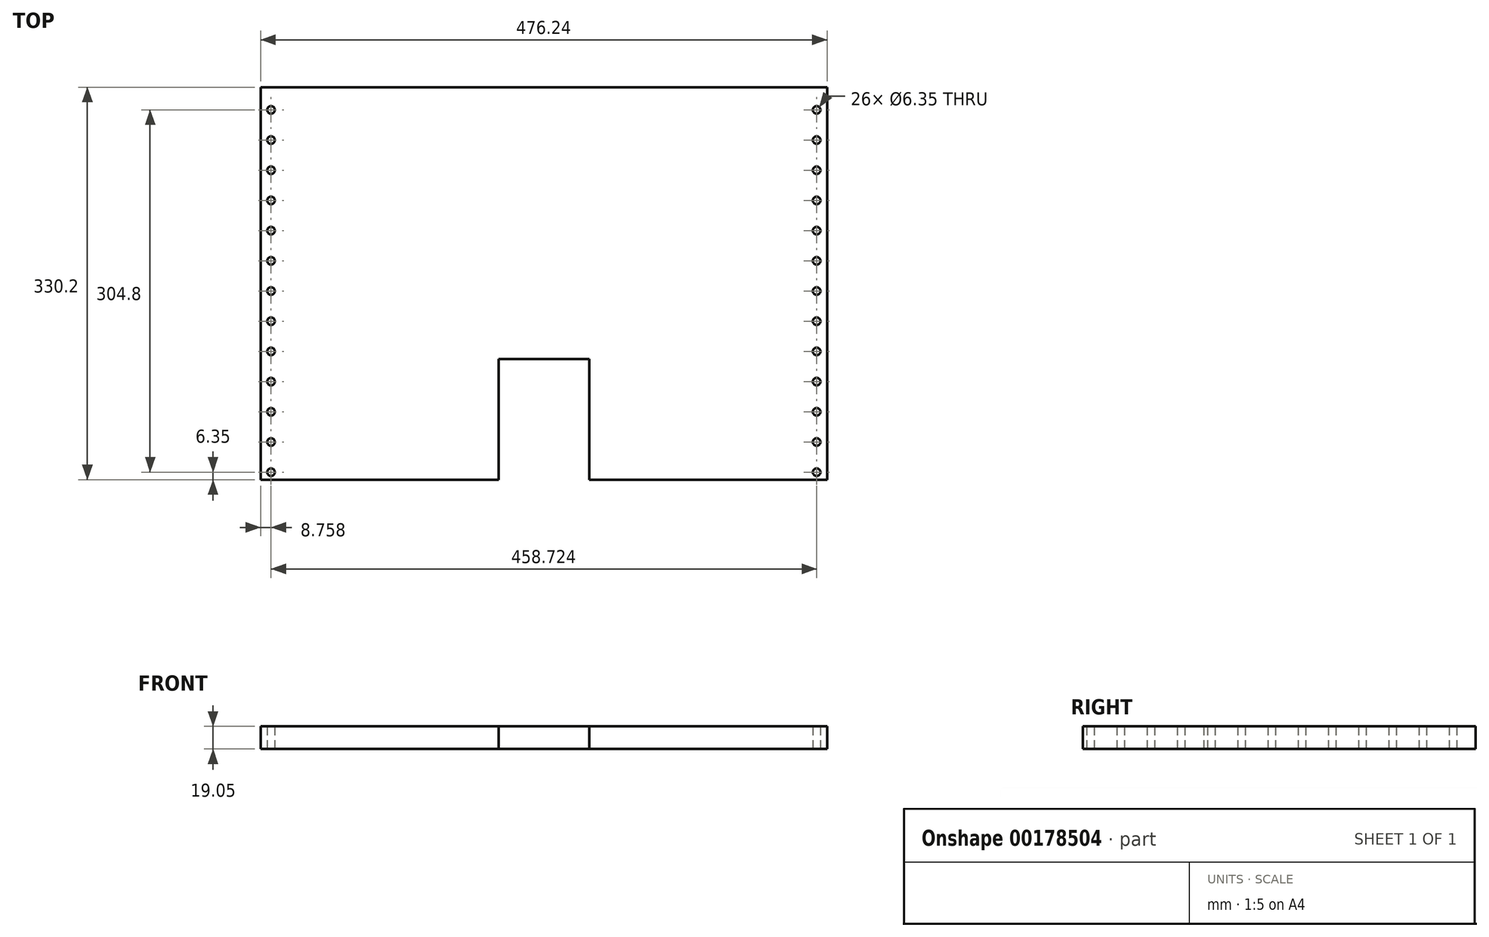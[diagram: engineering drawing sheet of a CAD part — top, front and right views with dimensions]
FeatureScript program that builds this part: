
annotation { "Feature Type Name" : "Feature", "Feature Type Description" : "" }
export const myFeature = defineFeature(function(context is Context, id is Id, definition is map)
    precondition{}
    {
        {
            var Q0;
            Q0=qCreatedBy(makeId("Top.planeOp"),FACE);
            var sketch = newSketch(context, id + "F0", { "sketchPlane" : qUnion([Q0])});
            skLineSegment(sketch, "E0.bottom", {"start": v(-238.13, 165.1) * mm, "end": v(238.13, 165.1) * mm});
            skLineSegment(sketch, "E0.top", {"start": v(-238.13, -165.1) * mm, "end": v(238.13, -165.1) * mm});
            skLineSegment(sketch, "E0.left", {"start": v(-238.13, 165.1) * mm, "end": v(-238.13, -165.1) * mm});
            skLineSegment(sketch, "E0.right", {"start": v(238.13, 165.1) * mm, "end": v(238.13, -165.1) * mm});
            skPoint(sketch, "E0.middle", {"position": v(0, 0) * mm});
            skPoint(sketch, "E1", {"position": v(0, 165.1) * mm});
            skLineSegment(sketch, "E2", {"start": v(0, 165.1) * mm, "end": v(0, -165.1) * mm});
            skLineSegment(sketch, "E3", {"start": v(0, -165.1) * mm, "end": v(-38.1, -165.1) * mm});
            skLineSegment(sketch, "E4", {"start": v(-38.1, -165.1) * mm, "end": v(-38.1, -63.5) * mm});
            skLineSegment(sketch, "E5", {"start": v(-38.1, -63.5) * mm, "end": v(0, -63.5) * mm});
            skLineSegment(sketch, "E6.MirrorCS", {"start": v(38.1, -63.5) * mm, "end": v(0, -63.5) * mm});
            skLineSegment(sketch, "E7.MirrorCS", {"start": v(38.1, -165.1) * mm, "end": v(38.1, -63.5) * mm});
            skLineSegment(sketch, "E8.MirrorCS", {"start": v(0, -165.1) * mm, "end": v(38.1, -165.1) * mm});
            skPoint(sketch, "E9", {"position": v(223.01, -165.1) * mm});
            skLineSegment(sketch, "E10", {"start": v(223.01, -165.1) * mm, "end": v(223.01, 165.1) * mm});
            skCircle(sketch, "E11", {"center": v(229.36, -158.75) * mm, "radius": 3.18 * mm});
            skCircle(sketch, "E12.0.1.0", {"center": v(229.36, -133.35) * mm, "radius": 3.18 * mm});
            skCircle(sketch, "E12.0.2.0", {"center": v(229.36, -107.95) * mm, "radius": 3.18 * mm});
            skCircle(sketch, "E12.0.3.0", {"center": v(229.36, -82.55) * mm, "radius": 3.18 * mm});
            skCircle(sketch, "E12.0.4.0", {"center": v(229.36, -57.15) * mm, "radius": 3.18 * mm});
            skCircle(sketch, "E12.0.5.0", {"center": v(229.36, -31.75) * mm, "radius": 3.18 * mm});
            skCircle(sketch, "E12.0.6.0", {"center": v(229.36, -6.35) * mm, "radius": 3.18 * mm});
            skCircle(sketch, "E12.0.7.0", {"center": v(229.36, 19.05) * mm, "radius": 3.18 * mm});
            skCircle(sketch, "E12.0.8.0", {"center": v(229.36, 44.45) * mm, "radius": 3.18 * mm});
            skCircle(sketch, "E12.0.9.0", {"center": v(229.36, 69.85) * mm, "radius": 3.18 * mm});
            skCircle(sketch, "E12.0.10.0", {"center": v(229.36, 95.25) * mm, "radius": 3.18 * mm});
            skCircle(sketch, "E12.0.11.0", {"center": v(229.36, 120.65) * mm, "radius": 3.18 * mm});
            skCircle(sketch, "E12.0.12.0", {"center": v(229.36, 146.05) * mm, "radius": 3.18 * mm});
            skLineSegment(sketch, "E12.direction1", {"start": v(229.36, -158.75) * mm, "end": v(254.76, -158.75) * mm, "construction": true});
            skLineSegment(sketch, "E12.direction2", {"start": v(229.36, -158.75) * mm, "end": v(229.36, -133.35) * mm, "construction": true});
            skCircle(sketch, "E13.MirrorC", {"center": v(-229.36, 146.05) * mm, "radius": 3.18 * mm});
            skCircle(sketch, "E14.MirrorC", {"center": v(-229.36, 120.65) * mm, "radius": 3.18 * mm});
            skCircle(sketch, "E15.MirrorC", {"center": v(-229.36, 95.25) * mm, "radius": 3.18 * mm});
            skCircle(sketch, "E16.MirrorC", {"center": v(-229.36, 69.85) * mm, "radius": 3.18 * mm});
            skCircle(sketch, "E17.MirrorC", {"center": v(-229.36, 44.45) * mm, "radius": 3.18 * mm});
            skCircle(sketch, "E18.MirrorC", {"center": v(-229.36, 19.05) * mm, "radius": 3.18 * mm});
            skCircle(sketch, "E19.MirrorC", {"center": v(-229.36, -6.35) * mm, "radius": 3.18 * mm});
            skCircle(sketch, "E20.MirrorC", {"center": v(-229.36, -31.75) * mm, "radius": 3.18 * mm});
            skCircle(sketch, "E21.MirrorC", {"center": v(-229.36, -57.15) * mm, "radius": 3.18 * mm});
            skCircle(sketch, "E22.MirrorC", {"center": v(-229.36, -82.55) * mm, "radius": 3.18 * mm});
            skCircle(sketch, "E23.MirrorC", {"center": v(-229.36, -107.95) * mm, "radius": 3.18 * mm});
            skCircle(sketch, "E24.MirrorC", {"center": v(-229.36, -133.35) * mm, "radius": 3.18 * mm});
            skCircle(sketch, "E25.MirrorC", {"center": v(-229.36, -158.75) * mm, "radius": 3.18 * mm});
            skSolve(sketch);
        }
        {
            var Q0;
            {var subQ4=sQuery(id+"F0.wireOp",EDGE,"E0.left");Q0=makeQuery(id+"F0.imprint","IMPRINT",FACE,{"disambiguationData":[TD([[makeQuery(id+"F0.imprint","IMPRINT",EDGE,{"derivedFrom":subQ4}),1.0]])]});}
            var Q1;
            {var subQ4=sQuery(id+"F0.wireOp",EDGE,"E0.right");Q1=makeQuery(id+"F0.imprint","IMPRINT",FACE,{"disambiguationData":[TD([[makeQuery(id+"F0.imprint","IMPRINT",EDGE,{"derivedFrom":subQ4}),-1.0]])]});}
            var Q2;
            {var subQ0=sQuery(id+"F0.wireOp",EDGE,"E6.MirrorCS");Q2=makeQuery(id+"F0.imprint","IMPRINT",FACE,{"disambiguationData":[TD([[makeQuery(id+"F0.imprint","IMPRINT",EDGE,{"derivedFrom":subQ0}),-1.0]])]});}
            extrude(context, id + "F1", {"entities" : qUnion([Q0, Q1, Q2]), "depth" : 19.05 * mm});
        }
    });
